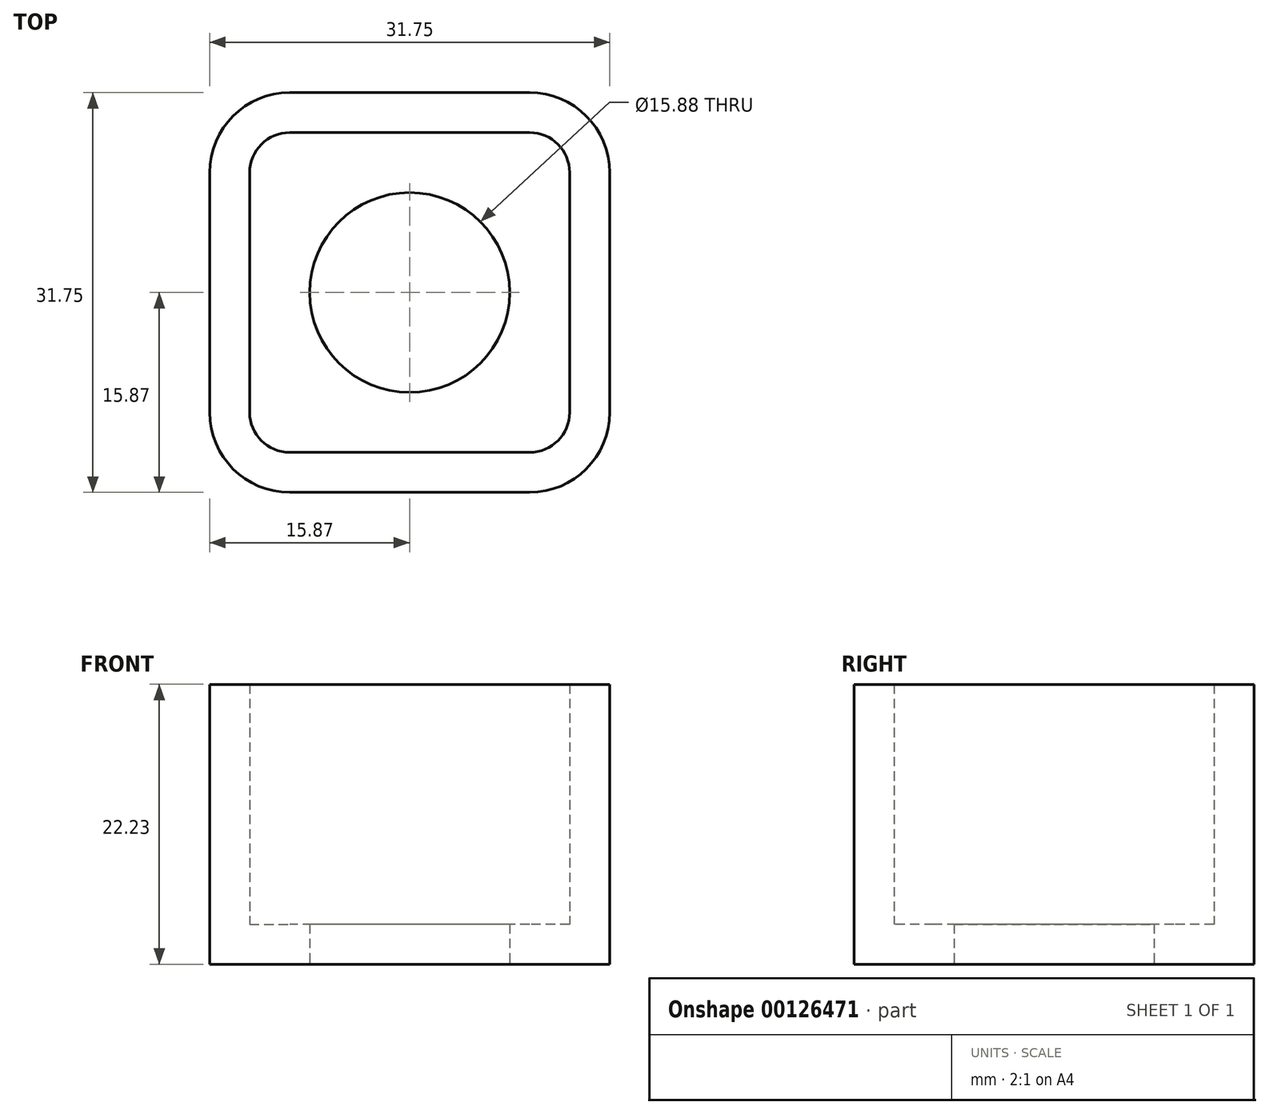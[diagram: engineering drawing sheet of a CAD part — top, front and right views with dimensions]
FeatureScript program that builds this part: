
annotation { "Feature Type Name" : "Feature", "Feature Type Description" : "" }
export const myFeature = defineFeature(function(context is Context, id is Id, definition is map)
    precondition{}
    {
        {
            var Q0;
            Q0=qCreatedBy(makeId("Top.planeOp"),FACE);
            var sketch = newSketch(context, id + "F0", { "sketchPlane" : qUnion([Q0])});
            skPoint(sketch, "E0", {"position": v(12.7, 12.7) * mm});
            skCircle(sketch, "E1", {"center": v(12.7, 12.7) * mm, "radius": 7.94 * mm});
            skLineSegment(sketch, "E2", {"start": v(0, 12.7) * mm, "end": v(0, 3.18) * mm});
            skLineSegment(sketch, "E3", {"start": v(3.18, 0) * mm, "end": v(12.7, 0) * mm});
            skPoint(sketch, "E4.visualSharp", {"position": v(0, 0) * mm});
            skArc(sketch, "E4.filletArc", {"start": v(0, 3.17) * mm, "mid": v(0.93, 0.93) * mm, "end": v(3.18, 0) * mm});
            skLineSegment(sketch, "E5", {"start": v(12.7, 12.7) * mm, "end": v(12.7, -3.18) * mm, "construction": true});
            skLineSegment(sketch, "E6", {"start": v(12.7, 12.7) * mm, "end": v(-3.18, 12.7) * mm, "construction": true});
            skLineSegment(sketch, "E7", {"start": v(-3.18, 12.7) * mm, "end": v(-3.18, 3.17) * mm});
            skLineSegment(sketch, "E8", {"start": v(3.18, -3.18) * mm, "end": v(12.7, -3.18) * mm});
            skPoint(sketch, "E9.visualSharp", {"position": v(-3.17, -3.18) * mm});
            skArc(sketch, "E9.filletArc", {"start": v(-3.18, 3.17) * mm, "mid": v(-1.32, -1.32) * mm, "end": v(3.18, -3.18) * mm});
            skLineSegment(sketch, "E10.MirrorCS", {"start": v(-3.18, 12.7) * mm, "end": v(-3.18, 22.23) * mm});
            skLineSegment(sketch, "E11.MirrorCS", {"start": v(0, 12.7) * mm, "end": v(0, 22.23) * mm});
            skArc(sketch, "E12.MirrorCS", {"start": v(-3.18, 22.23) * mm, "mid": v(-1.32, 26.72) * mm, "end": v(3.18, 28.58) * mm});
            skArc(sketch, "E13.MirrorCS", {"start": v(0, 22.23) * mm, "mid": v(0.93, 24.47) * mm, "end": v(3.18, 25.4) * mm});
            skLineSegment(sketch, "E14.MirrorCS", {"start": v(3.18, 25.4) * mm, "end": v(12.7, 25.4) * mm});
            skLineSegment(sketch, "E15.MirrorCS", {"start": v(3.18, 28.58) * mm, "end": v(12.7, 28.58) * mm});
            skLineSegment(sketch, "E16.MirrorCS", {"start": v(22.23, -3.17) * mm, "end": v(12.7, -3.17) * mm});
            skLineSegment(sketch, "E17.MirrorCS", {"start": v(22.23, 0) * mm, "end": v(12.7, 0) * mm});
            skArc(sketch, "E18.MirrorCS", {"start": v(25.4, 3.18) * mm, "mid": v(24.47, 0.93) * mm, "end": v(22.23, 0) * mm});
            skArc(sketch, "E19.MirrorCS", {"start": v(28.58, 3.18) * mm, "mid": v(26.72, -1.32) * mm, "end": v(22.23, -3.17) * mm});
            skLineSegment(sketch, "E20.MirrorCS", {"start": v(28.58, 12.7) * mm, "end": v(28.58, 3.18) * mm});
            skLineSegment(sketch, "E21.MirrorCS", {"start": v(25.4, 12.7) * mm, "end": v(25.4, 3.18) * mm});
            skLineSegment(sketch, "E22.MirrorCS", {"start": v(25.4, 12.7) * mm, "end": v(25.4, 22.23) * mm});
            skLineSegment(sketch, "E23.MirrorCS", {"start": v(28.58, 12.7) * mm, "end": v(28.58, 22.23) * mm});
            skArc(sketch, "E24.MirrorCS", {"start": v(25.4, 22.23) * mm, "mid": v(24.47, 24.47) * mm, "end": v(22.23, 25.4) * mm});
            skArc(sketch, "E25.MirrorCS", {"start": v(28.58, 22.23) * mm, "mid": v(26.72, 26.72) * mm, "end": v(22.22, 28.58) * mm});
            skLineSegment(sketch, "E26.MirrorCS", {"start": v(22.23, 28.58) * mm, "end": v(12.7, 28.58) * mm});
            skLineSegment(sketch, "E27.MirrorCS", {"start": v(22.22, 25.4) * mm, "end": v(12.7, 25.4) * mm});
            skSolve(sketch);
        }
        {
            var Q0;
            Q0 = qSketchRegion(id + "F0", true);
            extrude(context, id + "F1", {"entities" : qUnion([Q0]), "depth" : 22.22 * mm});
        }
        {
            var Q0;
            Q0=makeQuery(id+"F0.imprint","IMPRINT",FACE,{"disambiguationData":[TD([[makeQuery(id+"F0.imprint","IMPRINT",EDGE,{"derivedFrom":sQuery(id+"F0.wireOp",EDGE,"E1")}),-1.0]])]});
            extrude(context, id + "F2", {"entities" : qUnion([Q0]), "operationType" : NewBodyOperationType.ADD, "depth" : 3.17 * mm});
        }
    });
